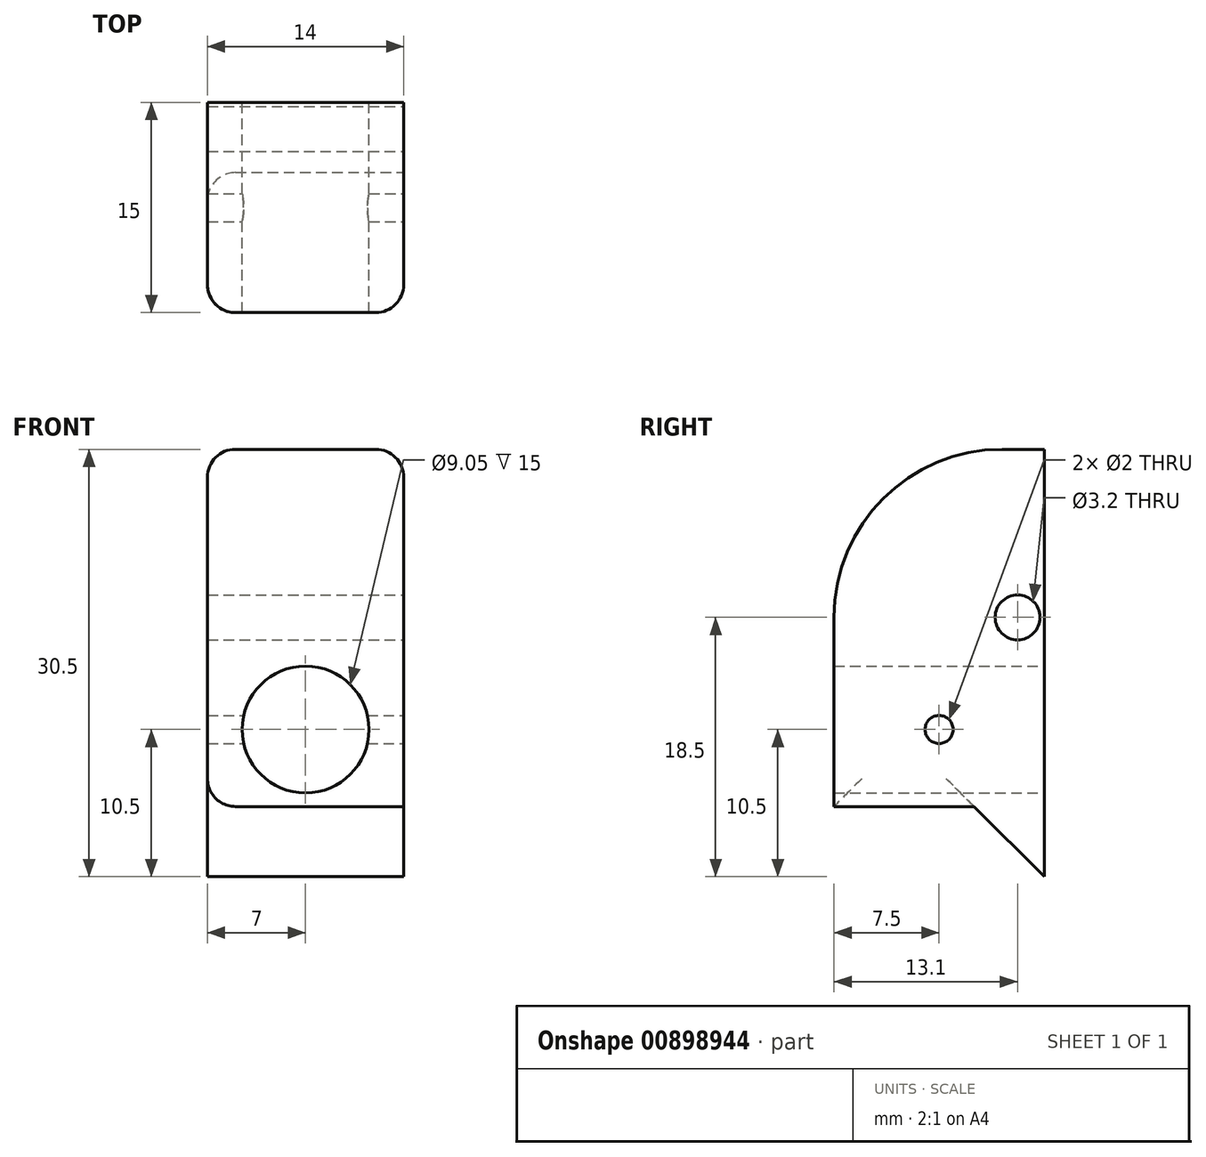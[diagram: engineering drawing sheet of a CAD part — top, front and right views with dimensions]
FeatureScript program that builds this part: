
annotation { "Feature Type Name" : "Feature", "Feature Type Description" : "" }
export const myFeature = defineFeature(function(context is Context, id is Id, definition is map)
    precondition{}
    {
        {
            var Q0;
            Q0=qCreatedBy(makeId("Front.planeOp"),FACE);
            var sketch = newSketch(context, id + "F0", { "sketchPlane" : qUnion([Q0])});
            skCircle(sketch, "E0", {"center": v(0, 0) * mm, "radius": 4.53 * mm});
            skLineSegment(sketch, "E1.bottom", {"start": v(-7, 20) * mm, "end": v(7, 20) * mm});
            skLineSegment(sketch, "E1.top", {"start": v(-7, -10.5) * mm, "end": v(7, -10.5) * mm});
            skLineSegment(sketch, "E1.left", {"start": v(-7, 20) * mm, "end": v(-7, -10.5) * mm});
            skLineSegment(sketch, "E1.right", {"start": v(7, 20) * mm, "end": v(7, -10.5) * mm});
            skSolve(sketch);
        }
        {
            var Q0;
            Q0=qSketchRegion(id+"F0",true);
            extrude(context, id + "F1", {"entities" : qUnion([Q0]), "depth" : 15 * mm, "offsetDistance" : 25 * mm});
        }
        {
            var Q0;
            Q0=makeQuery(id+"F1.opExtrude","SWEPT_FACE",FACE,{"disambiguationData":[OSD([sQuery(id+"F0.wireOp",EDGE,"E1.right")])]});
            var sketch = newSketch(context, id + "F2", { "sketchPlane" : qUnion([Q0])});
            skLineSegment(sketch, "E2", {"start": v(0, -10.5) * mm, "end": v(-5, -5.5) * mm});
            skLineSegment(sketch, "E3", {"start": v(-5, -5.5) * mm, "end": v(-15, -5.5) * mm});
            skLineSegment(sketch, "E4", {"start": v(-15, -5.5) * mm, "end": v(-15, -10.5) * mm});
            skLineSegment(sketch, "E5", {"start": v(-15, -10.5) * mm, "end": v(0, -10.5) * mm});
            skSolve(sketch);
        }
        {
            var Q0;
            Q0=qSketchRegion(id+"F2",true);
            extrude(context, id + "F3", {"entities" : qUnion([Q0]), "operationType" : NewBodyOperationType.REMOVE, "endBound" : BoundingType.THROUGH_ALL, "oppositeDirection" : true, "depth" : 25 * mm, "offsetDistance" : 25 * mm});
        }
        {
            var Q0;
            Q0=makeQuery(id+"F1.opExtrude","SWEPT_FACE",FACE,{"disambiguationData":[OSD([sQuery(id+"F0.wireOp",EDGE,"E1.right")])]});
            var sketch = newSketch(context, id + "F4", { "sketchPlane" : qUnion([Q0])});
            skCircle(sketch, "E6", {"center": v(-1.9, 8) * mm, "radius": 1.6 * mm});
            skCircle(sketch, "E7", {"center": v(-7.5, 0) * mm, "radius": 1 * mm});
            skSolve(sketch);
        }
        {
            var Q0;
            Q0=qSketchRegion(id+"F4",true);
            extrude(context, id + "F5", {"entities" : qUnion([Q0]), "operationType" : NewBodyOperationType.REMOVE, "endBound" : BoundingType.THROUGH_ALL, "oppositeDirection" : true, "depth" : 25 * mm, "offsetDistance" : 25 * mm});
        }
        {
            var Q0;
            Q0=makeQuery(id+"F1.opExtrude","CAP_EDGE",EDGE,{"disambiguationData":[OSD([sQuery(id+"F0.wireOp",EDGE,"E1.bottom")])],"isStart":false});
            fillet(context, id + "F6", {"entities" : qUnion([Q0]), "radius" : 12 * mm, "tangentPropagation" : true, "allowEdgeOverflow" : false});
        }
        {
            var Q0;
            Q0=makeQuery(id+"F3.boolean.opBoolean","COPY",EDGE,{"derivedFrom":makeQuery(id+"F3.opExtrude","SWEPT_EDGE",EDGE,{"disambiguationData":[OSD([sQuery(id+"F0.wireOp",EDGE,"E1.right"),sQuery(id+"F2.wireOp",EDGE,"E3"),sQuery(id+"F2.wireOp",EDGE,"E4")])]})});
            var Q1;
            Q1=makeQuery(id+"F1.opExtrude","CAP_EDGE",EDGE,{"disambiguationData":[OSD([sQuery(id+"F0.wireOp",EDGE,"E1.right")])],"isStart":false});
            var Q2;
            Q2=makeQuery(id+"F3.boolean.opBoolean","INTERSECT",EDGE,{"derivedFrom":[makeQuery(id+"F1.opExtrude","SWEPT_FACE",FACE,{"disambiguationData":[OSD([sQuery(id+"F0.wireOp",EDGE,"E1.left")])]}),makeQuery(id+"F3.opExtrude","SWEPT_FACE",FACE,{"disambiguationData":[OSD([sQuery(id+"F2.wireOp",EDGE,"E3")])]})]});
            var Q3;
            Q3=makeQuery(id+"F1.opExtrude","CAP_EDGE",EDGE,{"disambiguationData":[OSD([sQuery(id+"F0.wireOp",EDGE,"E1.left")])],"isStart":false});
            var Q4;
            Q4=makeQuery(id+"F6.opFillet","BLEND_EDGE",EDGE,{"blendedFrom":[makeQuery(id+"F1.opExtrude","CAP_EDGE",EDGE,{"disambiguationData":[OSD([sQuery(id+"F0.wireOp",EDGE,"E1.bottom")])],"isStart":false}),makeQuery(id+"F1.opExtrude","SWEPT_FACE",FACE,{"disambiguationData":[OSD([sQuery(id+"F0.wireOp",EDGE,"E1.left")])]})],"blendedInto":[makeQuery(id+"F1.opExtrude","SWEPT_FACE",FACE,{"disambiguationData":[OSD([sQuery(id+"F0.wireOp",EDGE,"E1.left")])]})]});
            var Q5;
            Q5=makeQuery(id+"F3.boolean.opBoolean","COPY",EDGE,{"derivedFrom":makeQuery(id+"F3.opExtrude","CAP_EDGE",EDGE,{"disambiguationData":[OSD([sQuery(id+"F2.wireOp",EDGE,"E3")])],"isStart":true})});
            fillet(context, id + "F7", {"entities" : qUnion([Q0, Q1, Q2, Q3, Q4, Q5]), "radius" : 2 * mm, "tangentPropagation" : true, "allowEdgeOverflow" : false});
        }
    });
